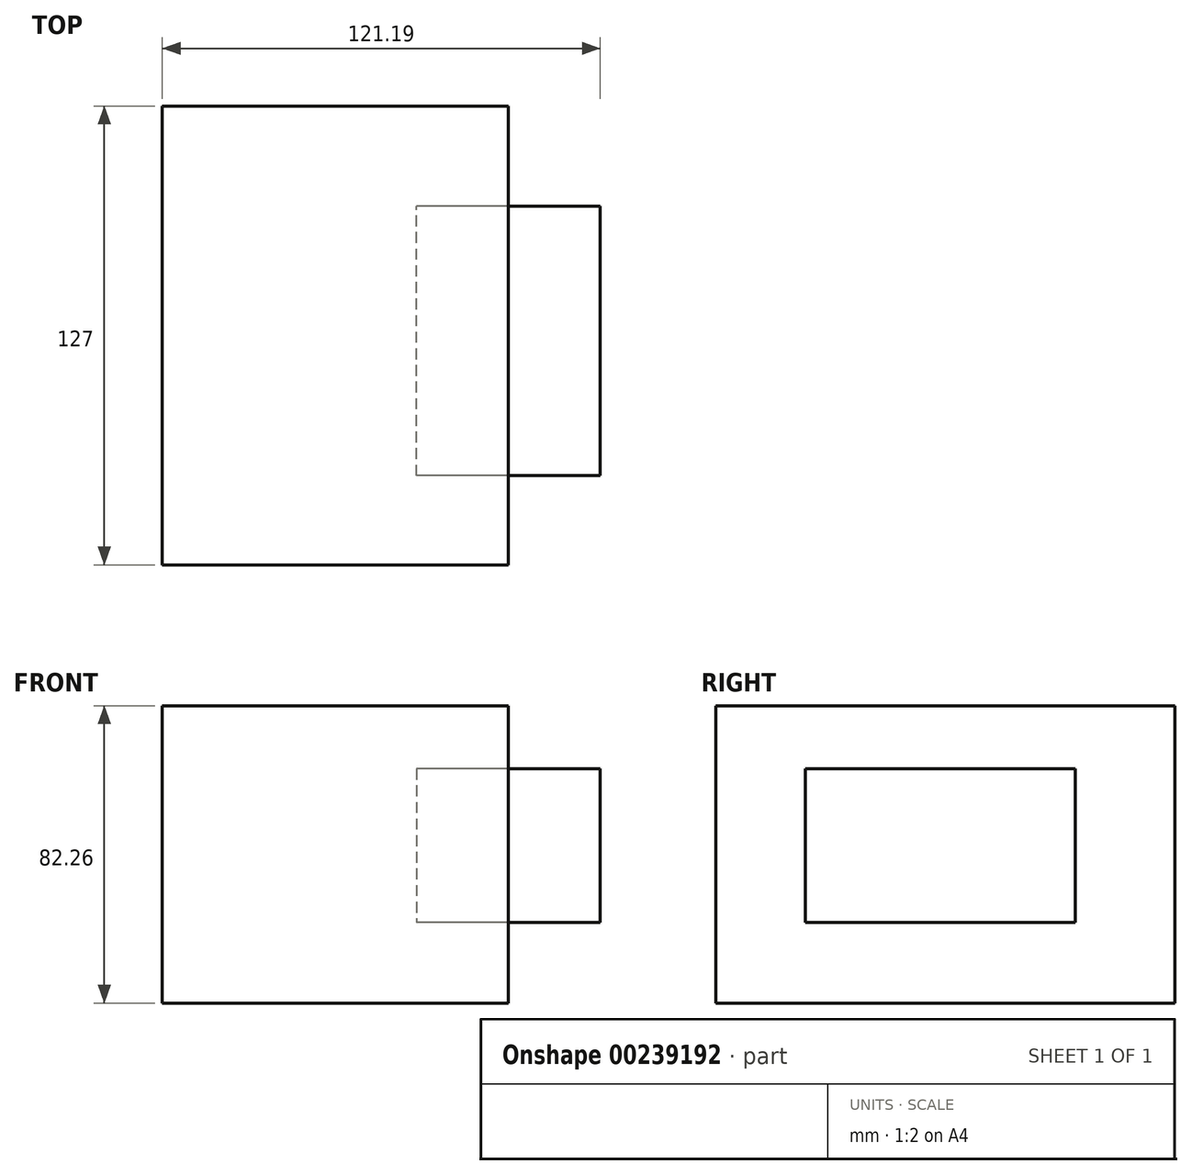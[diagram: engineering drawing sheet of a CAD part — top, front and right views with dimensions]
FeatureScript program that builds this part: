
annotation { "Feature Type Name" : "Feature", "Feature Type Description" : "" }
export const myFeature = defineFeature(function(context is Context, id is Id, definition is map)
    precondition{}
    {
        {
            var Q0;
            Q0=qCreatedBy(makeId("Front.planeOp"),FACE);
            var sketch = newSketch(context, id + "F0", { "sketchPlane" : qUnion([Q0])});
            skLineSegment(sketch, "E0.bottom", {"start": v(-38.4, 37.7) * mm, "end": v(57.39, 37.7) * mm});
            skLineSegment(sketch, "E0.top", {"start": v(-38.4, -44.56) * mm, "end": v(57.39, -44.56) * mm});
            skLineSegment(sketch, "E0.left", {"start": v(-38.4, 37.7) * mm, "end": v(-38.4, -44.56) * mm});
            skLineSegment(sketch, "E0.right", {"start": v(57.39, 37.7) * mm, "end": v(57.39, -44.56) * mm});
            skSolve(sketch);
        }
        {
            var Q0;
            Q0 = qSketchRegion(id + "F0", true);
            extrude(context, id + "F1", {"entities" : qUnion([Q0]), "endBound" : BoundingType.SYMMETRIC, "depth" : 127 * mm});
        }
        {
            var Q0;
            Q0=makeQuery(id+"F1.opExtrude","SWEPT_FACE",FACE,{"disambiguationData":[OSD([sQuery(id+"F0.wireOp",EDGE,"E0.right")])]});
            var sketch = newSketch(context, id + "F2", { "sketchPlane" : qUnion([Q0])});
            skLineSegment(sketch, "E1.bottom", {"start": v(-38.78, 20.27) * mm, "end": v(35.84, 20.27) * mm});
            skLineSegment(sketch, "E1.top", {"start": v(-38.78, -22.23) * mm, "end": v(35.84, -22.23) * mm});
            skLineSegment(sketch, "E1.left", {"start": v(-38.78, 20.27) * mm, "end": v(-38.78, -22.23) * mm});
            skLineSegment(sketch, "E1.right", {"start": v(35.84, 20.27) * mm, "end": v(35.84, -22.23) * mm});
            skSolve(sketch);
        }
        {
            var Q0;
            Q0 = qSketchRegion(id + "F2", true);
            extrude(context, id + "F3", {"entities" : qUnion([Q0]), "endBound" : BoundingType.SYMMETRIC, "depth" : 50.8 * mm});
        }
    });
